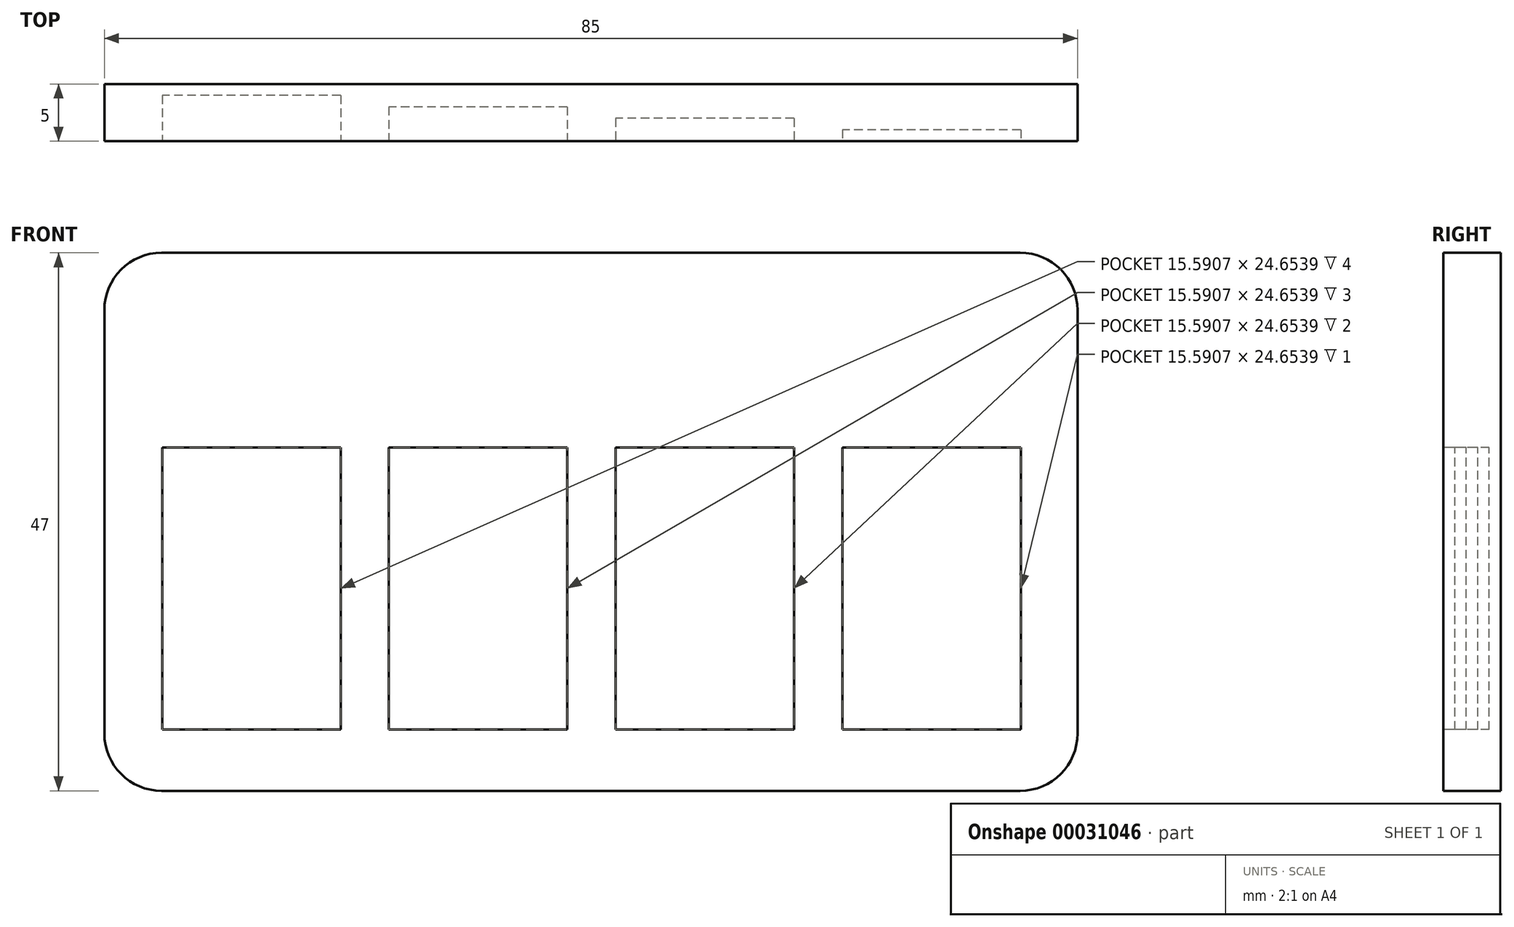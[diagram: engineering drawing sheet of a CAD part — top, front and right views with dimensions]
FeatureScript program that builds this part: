
annotation { "Feature Type Name" : "Feature", "Feature Type Description" : "" }
export const myFeature = defineFeature(function(context is Context, id is Id, definition is map)
    precondition{}
    {
        {
            var Q0;
            Q0=qCreatedBy(makeId("Front.planeOp"),FACE);
            var sketch = newSketch(context, id + "F0", { "sketchPlane" : qUnion([Q0])});
            skLineSegment(sketch, "E0.rect.bottom", {"start": v(37.5, -23.5) * mm, "end": v(-37.5, -23.5) * mm});
            skLineSegment(sketch, "E0.rect.top", {"start": v(37.5, 23.5) * mm, "end": v(-37.5, 23.5) * mm});
            skLineSegment(sketch, "E0.rect.left", {"start": v(42.5, -18.5) * mm, "end": v(42.5, 18.5) * mm});
            skLineSegment(sketch, "E0.rect.right", {"start": v(-42.5, -18.5) * mm, "end": v(-42.5, 18.5) * mm});
            skPoint(sketch, "E0.rect.middle", {"position": v(0, 0) * mm});
            skPoint(sketch, "E1.visualSharp", {"position": v(-42.5, 23.5) * mm});
            skArc(sketch, "E1.filletArc", {"start": v(-37.5, 23.5) * mm, "mid": v(-41.04, 22.04) * mm, "end": v(-42.5, 18.5) * mm});
            skPoint(sketch, "E2.visualSharp", {"position": v(42.5, 23.5) * mm});
            skArc(sketch, "E2.filletArc", {"start": v(42.5, 18.5) * mm, "mid": v(41.04, 22.04) * mm, "end": v(37.5, 23.5) * mm});
            skPoint(sketch, "E3.visualSharp", {"position": v(42.5, -23.5) * mm});
            skArc(sketch, "E3.filletArc", {"start": v(37.5, -23.5) * mm, "mid": v(41.04, -22.04) * mm, "end": v(42.5, -18.5) * mm});
            skPoint(sketch, "E4.visualSharp", {"position": v(-42.5, -23.5) * mm});
            skArc(sketch, "E4.filletArc", {"start": v(-42.5, -18.5) * mm, "mid": v(-41.04, -22.04) * mm, "end": v(-37.5, -23.5) * mm});
            skSolve(sketch);
        }
        {
            var Q0;
            Q0 = qSketchRegion(id + "F0", true);
            extrude(context, id + "F1", {"entities" : qUnion([Q0]), "depth" : 5 * mm});
        }
        {
            var Q0;
            {var subQ0=sQuery(id+"F0.wireOp",EDGE,"E0.rect.bottom");var subQ1=sQuery(id+"F0.wireOp",EDGE,"E0.rect.top");var subQ2=sQuery(id+"F0.wireOp",EDGE,"E0.rect.left");var subQ3=sQuery(id+"F0.wireOp",EDGE,"E0.rect.right");var subQ4=sQuery(id+"F0.wireOp",EDGE,"E1.filletArc");var subQ5=sQuery(id+"F0.wireOp",EDGE,"E2.filletArc");var subQ6=sQuery(id+"F0.wireOp",EDGE,"E3.filletArc");var subQ7=sQuery(id+"F0.wireOp",EDGE,"E4.filletArc");Q0=makeQuery(id+"FCLWlvzxLRd8ehp_1.boolean.opBoolean","SPLIT",FACE,{"disambiguationData":[TD([makeQuery(id+"F1.opExtrude","SWEPT_FACE",FACE,{"disambiguationData":[OSD([subQ0])]})])],"derivedFrom":makeQuery(id+"F1.opExtrude","CAP_FACE",FACE,{"disambiguationData":[OSD([subQ0,subQ1,subQ2,subQ3,subQ4,subQ5,subQ6,subQ7])],"isStart":false})});}
            var sketch = newSketch(context, id + "F2", { "sketchPlane" : qUnion([Q0])});
            skLineSegment(sketch, "E5", {"start": v(-37.5, 23.5) * mm, "end": v(-37.5, -23.5) * mm, "construction": true});
            skLineSegment(sketch, "E6", {"start": v(-36.64, 12.23) * mm, "end": v(37.5, 12.23) * mm, "construction": true});
            skLineSegment(sketch, "E7", {"start": v(-42.5, -18.5) * mm, "end": v(42.5, -18.5) * mm, "construction": true});
            skLineSegment(sketch, "E8", {"start": v(-36.64, -5.83) * mm, "end": v(37.5, -5.83) * mm, "construction": true});
            skLineSegment(sketch, "E9", {"start": v(-36.64, -5.83) * mm, "end": v(-37.5, -5.83) * mm, "construction": true});
            skLineSegment(sketch, "E10", {"start": v(37.5, 23.5) * mm, "end": v(37.5, -23.5) * mm, "construction": true});
            skLineSegment(sketch, "E11.rect.bottom", {"start": v(-21.86, -18.15) * mm, "end": v(-37.45, -18.15) * mm});
            skLineSegment(sketch, "E11.rect.top", {"start": v(-21.86, 6.5) * mm, "end": v(-37.45, 6.5) * mm});
            skLineSegment(sketch, "E11.rect.left", {"start": v(-21.86, -18.15) * mm, "end": v(-21.86, 6.5) * mm});
            skLineSegment(sketch, "E11.rect.right", {"start": v(-37.45, -18.15) * mm, "end": v(-37.45, 6.5) * mm});
            skPoint(sketch, "E11.rect.middle", {"position": v(-29.65, -5.83) * mm});
            skLineSegment(sketch, "E12.1.0.0", {"start": v(-2.06, -18.15) * mm, "end": v(-2.06, 6.5) * mm});
            skLineSegment(sketch, "E12.1.0.1", {"start": v(-2.06, 6.5) * mm, "end": v(-17.65, 6.5) * mm});
            skLineSegment(sketch, "E12.1.0.2", {"start": v(-17.65, -18.15) * mm, "end": v(-17.65, 6.5) * mm});
            skLineSegment(sketch, "E12.1.0.3", {"start": v(-2.06, -18.15) * mm, "end": v(-17.65, -18.15) * mm});
            skLineSegment(sketch, "E12.2.0.0", {"start": v(17.74, -18.15) * mm, "end": v(17.74, 6.5) * mm});
            skLineSegment(sketch, "E12.2.0.1", {"start": v(17.74, 6.5) * mm, "end": v(2.15, 6.5) * mm});
            skLineSegment(sketch, "E12.2.0.2", {"start": v(2.15, -18.15) * mm, "end": v(2.15, 6.5) * mm});
            skLineSegment(sketch, "E12.2.0.3", {"start": v(17.74, -18.15) * mm, "end": v(2.15, -18.15) * mm});
            skLineSegment(sketch, "E12.3.0.0", {"start": v(37.54, -18.15) * mm, "end": v(37.54, 6.5) * mm});
            skLineSegment(sketch, "E12.3.0.1", {"start": v(37.54, 6.5) * mm, "end": v(21.95, 6.5) * mm});
            skLineSegment(sketch, "E12.3.0.2", {"start": v(21.95, -18.15) * mm, "end": v(21.95, 6.5) * mm});
            skLineSegment(sketch, "E12.3.0.3", {"start": v(37.54, -18.15) * mm, "end": v(21.95, -18.15) * mm});
            skLineSegment(sketch, "E12.direction1", {"start": v(-21.86, -18.15) * mm, "end": v(-2.06, -18.15) * mm, "construction": true});
            skSolve(sketch);
        }
        {
            var Q0;
            Q0=makeQuery(id+"F2.imprint","IMPRINT",FACE,{"disambiguationData":[TD([[makeQuery(id+"F2.imprint","IMPRINT",EDGE,{"derivedFrom":sQuery(id+"F2.wireOp",EDGE,"E11.rect.bottom")}),-1.0]])]});
            extrude(context, id + "F3", {"entities" : qUnion([Q0]), "operationType" : NewBodyOperationType.REMOVE, "oppositeDirection" : true, "depth" : 4 * mm});
        }
        {
            var Q0;
            Q0=makeQuery(id+"F2.imprint","IMPRINT",FACE,{"disambiguationData":[TD([[makeQuery(id+"F2.imprint","IMPRINT",EDGE,{"derivedFrom":sQuery(id+"F2.wireOp",EDGE,"E12.1.0.0")}),1.0]])]});
            extrude(context, id + "F4", {"entities" : qUnion([Q0]), "operationType" : NewBodyOperationType.REMOVE, "oppositeDirection" : true, "depth" : 3 * mm});
        }
        {
            var Q0;
            Q0=makeQuery(id+"F2.imprint","IMPRINT",FACE,{"disambiguationData":[TD([[makeQuery(id+"F2.imprint","IMPRINT",EDGE,{"derivedFrom":sQuery(id+"F2.wireOp",EDGE,"E12.2.0.0")}),1.0]])]});
            extrude(context, id + "F5", {"entities" : qUnion([Q0]), "operationType" : NewBodyOperationType.REMOVE, "oppositeDirection" : true, "depth" : 2 * mm});
        }
        {
            var Q0;
            Q0=makeQuery(id+"F2.imprint","IMPRINT",FACE,{"disambiguationData":[TD([[makeQuery(id+"F2.imprint","IMPRINT",EDGE,{"derivedFrom":sQuery(id+"F2.wireOp",EDGE,"E12.3.0.0")}),1.0]])]});
            extrude(context, id + "F6", {"entities" : qUnion([Q0]), "operationType" : NewBodyOperationType.REMOVE, "oppositeDirection" : true, "depth" : 1 * mm});
        }
    });
